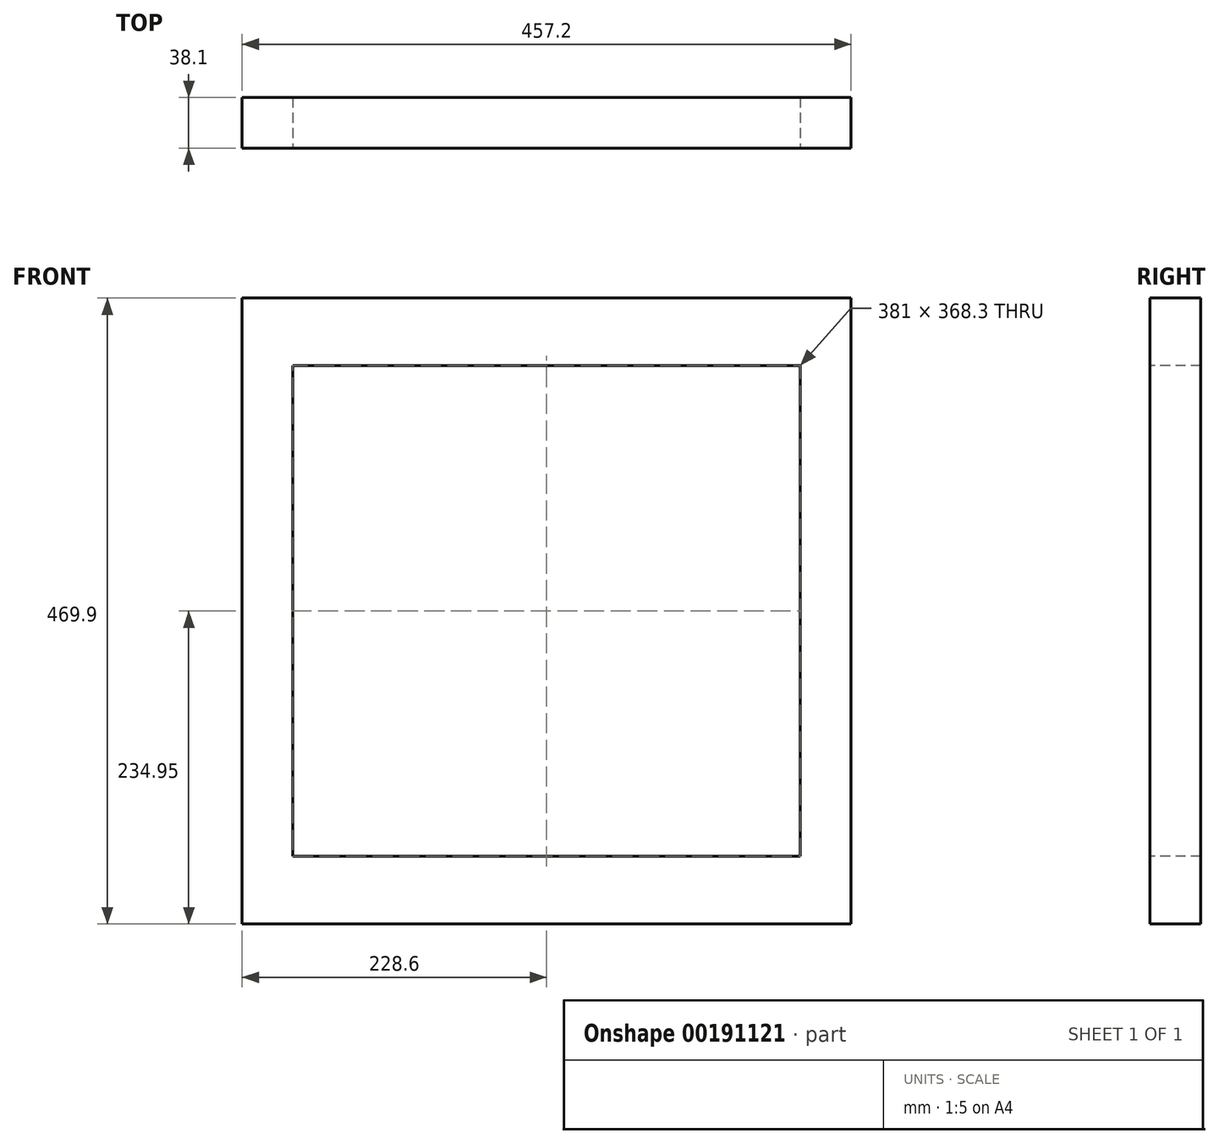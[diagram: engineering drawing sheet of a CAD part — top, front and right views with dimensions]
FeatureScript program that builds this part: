
annotation { "Feature Type Name" : "Feature", "Feature Type Description" : "" }
export const myFeature = defineFeature(function(context is Context, id is Id, definition is map)
    precondition{}
    {
        {
            var Q0;
            Q0=qCreatedBy(makeId("Front.planeOp"),FACE);
            var sketch = newSketch(context, id + "F0", { "sketchPlane" : qUnion([Q0])});
            skLineSegment(sketch, "E0.bottom", {"start": v(228.6, 234.95) * mm, "end": v(-228.6, 234.95) * mm});
            skLineSegment(sketch, "E0.top", {"start": v(228.6, -234.95) * mm, "end": v(-228.6, -234.95) * mm});
            skLineSegment(sketch, "E0.left", {"start": v(228.6, 234.95) * mm, "end": v(228.6, -234.95) * mm});
            skLineSegment(sketch, "E0.right", {"start": v(-228.6, 234.95) * mm, "end": v(-228.6, -234.95) * mm});
            skPoint(sketch, "E0.middle", {"position": v(0, 0) * mm});
            skSolve(sketch);
        }
        {
            var Q0;
            Q0 = qSketchRegion(id + "F0", true);
            extrude(context, id + "F1", {"entities" : qUnion([Q0]), "depth" : 38.1 * mm});
        }
        {
            var Q0;
            Q0=makeQuery(id+"F1.opExtrude","CAP_FACE",FACE,{"disambiguationData":[OSD([sQuery(id+"F0.wireOp",EDGE,"E0.bottom"),sQuery(id+"F0.wireOp",EDGE,"E0.top"),sQuery(id+"F0.wireOp",EDGE,"E0.left"),sQuery(id+"F0.wireOp",EDGE,"E0.right")])],"isStart":false});
            var sketch = newSketch(context, id + "F2", { "sketchPlane" : qUnion([Q0])});
            skLineSegment(sketch, "E1.bottom", {"start": v(190.5, 184.15) * mm, "end": v(-190.5, 184.15) * mm});
            skLineSegment(sketch, "E1.top", {"start": v(190.5, -184.15) * mm, "end": v(-190.5, -184.15) * mm});
            skLineSegment(sketch, "E1.left", {"start": v(190.5, 184.15) * mm, "end": v(190.5, -184.15) * mm});
            skLineSegment(sketch, "E1.right", {"start": v(-190.5, 184.15) * mm, "end": v(-190.5, -184.15) * mm});
            skPoint(sketch, "E1.middle", {"position": v(0, 0) * mm});
            skSolve(sketch);
        }
        {
            var Q0;
            Q0 = qSketchRegion(id + "F2", true);
            extrude(context, id + "F3", {"entities" : qUnion([Q0]), "operationType" : NewBodyOperationType.REMOVE, "endBound" : BoundingType.THROUGH_ALL, "oppositeDirection" : true, "depth" : 25.4 * mm});
        }
    });
